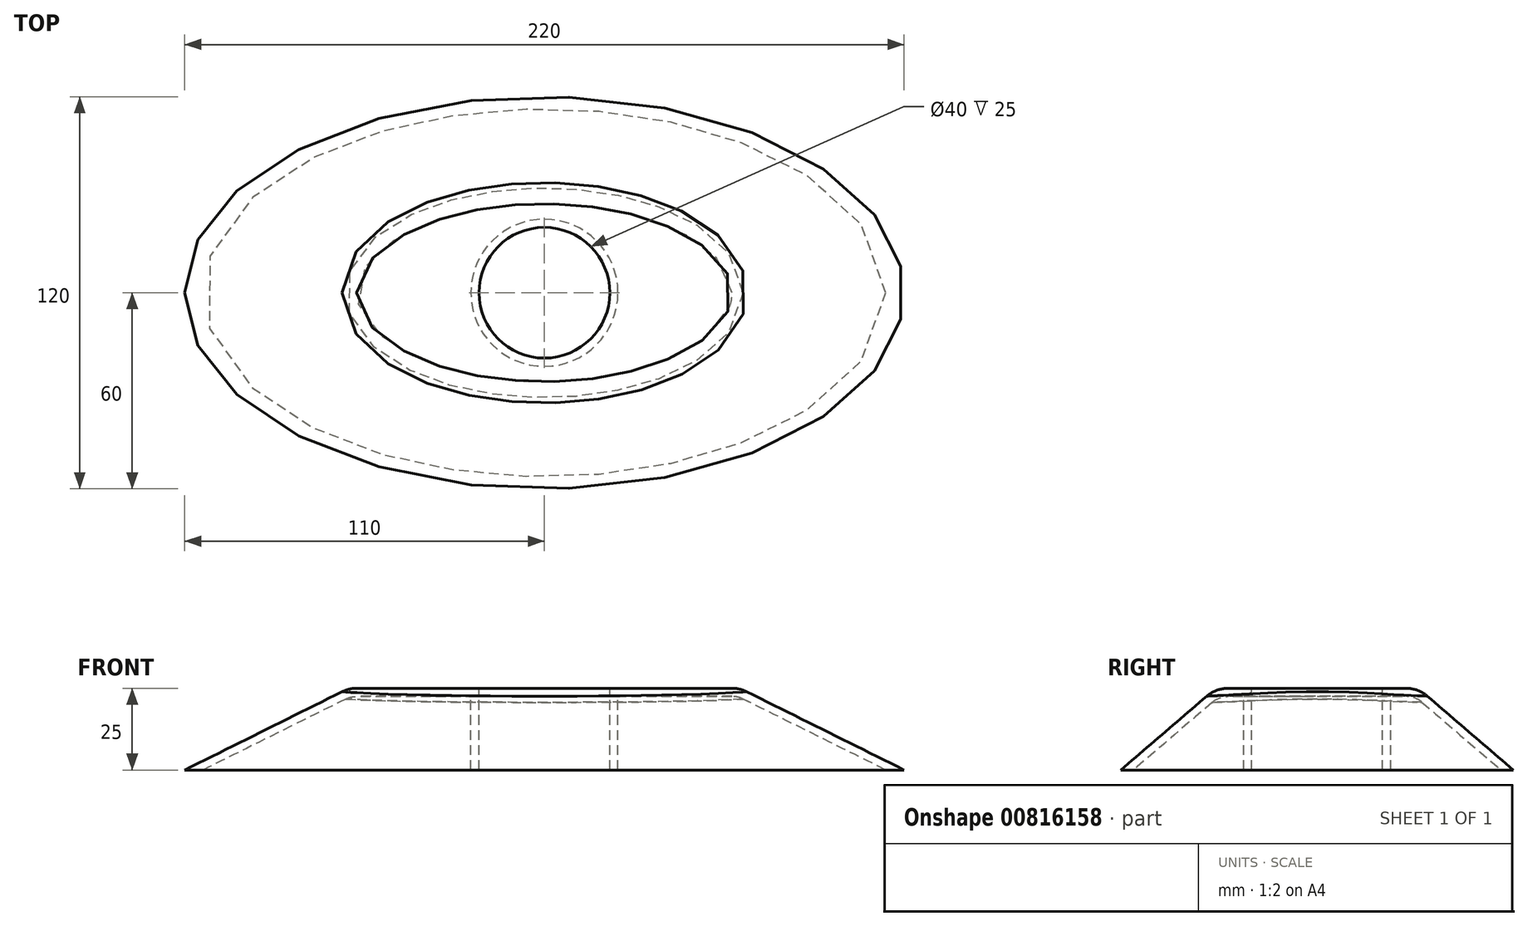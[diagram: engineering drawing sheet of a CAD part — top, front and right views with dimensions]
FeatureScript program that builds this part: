
annotation { "Feature Type Name" : "Feature", "Feature Type Description" : "" }
export const myFeature = defineFeature(function(context is Context, id is Id, definition is map)
    precondition{}
    {
        {
            var Q0;
            Q0=qCreatedBy(makeId("Top.planeOp"),FACE);
            var sketch = newSketch(context, id + "F0", { "sketchPlane" : qUnion([Q0])});
            skEllipse(sketch, "E0", {"center": v(0, 0) * mm, "majorRadius": 110 * mm, "minorRadius": 60 * mm, "majorAxis": v(-1, 0)});
            skSolve(sketch);
        }
        {
            var Q0;
            Q0=qCreatedBy(makeId("Top.planeOp"),FACE);
            cPlane(context, id + "F1", {"entities" : qUnion([Q0]), "cplaneType" : CPlaneType.OFFSET, "offset" : 25 * mm, "width" : 150 * mm, "height" : 150 * mm});
        }
        {
            var Q0;
            Q0=qCreatedBy(id+"F1.planeOp",FACE);
            var sketch = newSketch(context, id + "F2", { "sketchPlane" : qUnion([Q0])});
            skEllipse(sketch, "E1", {"center": v(0, 0) * mm, "majorRadius": 59.74 * mm, "minorRadius": 30.9 * mm, "majorAxis": v(-1, 0)});
            skSolve(sketch);
        }
        {
            var Q0;
            Q0=makeQuery(id+"F0.imprint","IMPRINT",FACE,{"disambiguationData":[TD([[makeQuery(id+"F0.imprint","IMPRINT",EDGE,{"derivedFrom":sQuery(id+"F0.wireOp",EDGE,"E0")}),1.0]])]});
            var Q1;
            Q1=makeQuery(id+"F2.imprint","IMPRINT",FACE,{"disambiguationData":[TD([[makeQuery(id+"F2.imprint","IMPRINT",EDGE,{"derivedFrom":sQuery(id+"F2.wireOp",EDGE,"E1")}),1.0]])]});
            loft(context, id + "F3", {"sheetProfilesArray" : [{ "sheetProfileEntities" : qUnion([Q0]) }, { "sheetProfileEntities" : qUnion([Q1]) }]});
        }
        {
            var Q0;
            Q0=makeQuery(id+"F3.opLoft","CAP_FACE",FACE,{"disambiguationData":[OSD([makeQuery(id+"F2.imprint","IMPRINT",FACE,{"disambiguationData":[TD([[makeQuery(id+"F2.imprint","IMPRINT",EDGE,{"derivedFrom":sQuery(id+"F2.wireOp",EDGE,"E1")}),1.0]])]})])],"isStart":true});
            var sketch = newSketch(context, id + "F4", { "sketchPlane" : qUnion([Q0])});
            skCircle(sketch, "E2", {"center": v(0, 0) * mm, "radius": 20 * mm});
            skSolve(sketch);
        }
        {
            var Q0;
            Q0=makeQuery(id+"F4.imprint","IMPRINT",FACE,{"disambiguationData":[TD([[makeQuery(id+"F4.imprint","IMPRINT",EDGE,{"derivedFrom":sQuery(id+"F4.wireOp",EDGE,"E2")}),1.0]])]});
            extrude(context, id + "F5", {"entities" : qUnion([Q0]), "operationType" : NewBodyOperationType.REMOVE, "oppositeDirection" : true, "depth" : 25 * mm, "offsetDistance" : 25 * mm});
        }
        {
            var Q0;
            Q0=makeQuery(id+"F3.opLoft","MID_CAP_EDGE",EDGE,{"disambiguationData":[OSD([sQuery(id+"F2.wireOp",EDGE,"E1")])],"capPos":1.0});
            fillet(context, id + "F6", {"entities" : qUnion([Q0]), "radius" : 10 * mm, "tangentPropagation" : true, "allowEdgeOverflow" : false});
        }
        {
            var Q0;
            Q0=makeQuery(id+"F3.opLoft","CAP_FACE",FACE,{"disambiguationData":[OSD([makeQuery(id+"F0.imprint","IMPRINT",FACE,{"disambiguationData":[TD([[makeQuery(id+"F0.imprint","IMPRINT",EDGE,{"derivedFrom":sQuery(id+"F0.wireOp",EDGE,"E0")}),1.0]])]})])],"isStart":true});
            shell(context, id + "F7", {"entities" : qUnion([Q0]), "thickness" : 2.5 * mm});
        }
    });
